# Revit family: IS_Ceraplan_BD284_BIM_NL
name_source: partatom
category: Plumbing Fixtures
units: mm (PartAtom-declared; Revit-internal decimal feet)

## family parameters
Cut with Voids When Loaded = No
Host = Face
Maintain Annotation Orientation = No
OmniClass Number = 23.45.55.17
OmniClass Title = Mixing Faucets
Part Type = Normal
Room Calculation Point = No
Round Connector Dimension = Use Diameter
Shared = Yes

## types (2) — shared parameters
Accessories = https://www.idealstandard.nl
AreaUnits = millimeter
Assembly Code = C1030200
BIMObjectName = IS_IdealStandard_Washbasintaps_Ceraplan_BD284
BIMobject category = Sanitary
BIMobject main category = Taps & Mixers
BREEAMApproved = No
Brand = Ideal Standard
Brand url = https://www.idealstandard.nl
ConnectionType = Plumbing
CurrencyUnit = €
CurrentRevision = 1
Date of publishing = 2024-03-15
Default Elevation = 800 mm  [stored 2.62467 ft]
Description = CERAPLAN | Toiletkraan 42x81x56 mm, 5 l/min (3 bar), zonder waste
Design country = Italy
DurationUnit = jaar
ECA = No
EPD = https://www.idealstandard.nl
ExpectedLife = 30
FaucetFunction = MIXED
FaucetOperation = LEVERHANDLE
FaucetType = PILLAR
FlowRate = 5 l/min (3 bar)
Help = https://www.idealstandard.nl
IFC Classification = IfcValveType
IfcExportAs = IfcValveType
IfcExportType = FAUCET
InstallationInstructions = https://www.idealstandard.nl
LinearUnits = millimeter
Manufacturer = https://www.idealstandard.nl
Manufacturer name = Ideal Standard
ManufacturerURL = https://www.idealstandard.nl
Material = messing
Material main = Brass
ModelReference = CERAPLAN | Toiletkraan 42x81x56 mm, 5 l/min (3 bar), zonder waste
NBS Reference Code = 45-35-70/371
NBS Reference Description = Water supply fittings for wash basins and troughs
NBSDescription = Water supply fittings for wash basins and troughs
NBSReference = 45-35-70/371
Name = Washbasintaps_Ceraplan_BD284_IdealStandard
NettWeight = 0.93 Kg
NominalHeight = 116 mm  [stored 0.380577 ft]
NominalLength = 116 mm  [stored 0.380577 ft]
NominalWidth = 42 mm  [stored 0.137795 ft]
OmniClass Code = 23-31 11 00
OmniClass Description = Fauces
Product SKU = BD284
Product data url = https://www.idealstandard.nl
Product family = Ceraplan
Product name = CERAPLAN Basin pillar tap 116 mm. chrome
Product url = https://www.idealstandard.nl
ProductInformation = https://www.idealstandard.nl
QR code = http://bimobject.com
Shape = Vierkant / geometrisch
Size = 42 x 116 x 116 mm
Space = Intern
SpareParts = https://www.idealstandard.nl
TMV3 = Yes
Technical description = https://www.idealstandard.nl
TestPressure = 10 Bar
UNSPSC Code = 301815
URL = https://www.idealstandard.nl
Uniclass 2.0 Code = PR-35-79-85
Uniclass 2.0 Description = Wash Basin and Trough Water Supply Fittings
Uniclass2 = Pr_40_20_87_98
Uniclass2015Code = Pr_40_20_87_98
Uniclass2015Description = Washbasin taps
Uniclass2015Reference = Pr_40_20_87_98  Washbasin taps
Uniclass2015Title = Washbasin taps
Uniclass2015Version = Products v1.33
ValveMechanism = Pillar tap
ValveOperation = Single Lever
Version = 1
VolumeUnits = Liter
WRAS = Yes
WarrantyDescription = Fabrikanten Garantie
WarrantyDurationParts = 5
WarrantyDurationUnit = jaar
WarrantyGuarantorParts = https://www.idealstandard.nl
WaterEfficientProduct = No
WorkingPressure = 3 Bar
Youtube clip = https://www.youtube.com
zero-valued in all types: CWFU, Cost, HWFU, WFU

## per-type parameters (varying)
| type | BarCode | Color | Features | Finish | GTIN code | MAT | Model | ModelNumber |
| BD284AA - CERAPLAN BSN PLR TAP CLD/WTR G1/2 - Chrome | 3800861106890 | Chrome | CERAPLAN / Toiletkraan 42x81x56 mm in chroom afwerking, 5 l/min (3 bar), zonder waste / SmartShine | chroom | 3800861106890 | Chrome_Polished | BD284AA | BD284AA |
| BD284XG - CERAPLAN BSN PLR TAP CLD/WTR G1/2 - Matt Black | 3800861116875 | matzwart | CERAPLAN / Toiletkraan 42x81x56 mm in matzwart afwerking, 5 l/min (3 bar), zonder waste | matzwart | 3800861116875 | Silk Black | BD284XG | BD284XG |

note: [stored X ft] marks values corroborated as IEEE doubles in the binary element streams (Revit-internal decimal feet)

## geometry (parser evidence)
native form markers: Sweep x4
no freeform markers — native parametric forms only
